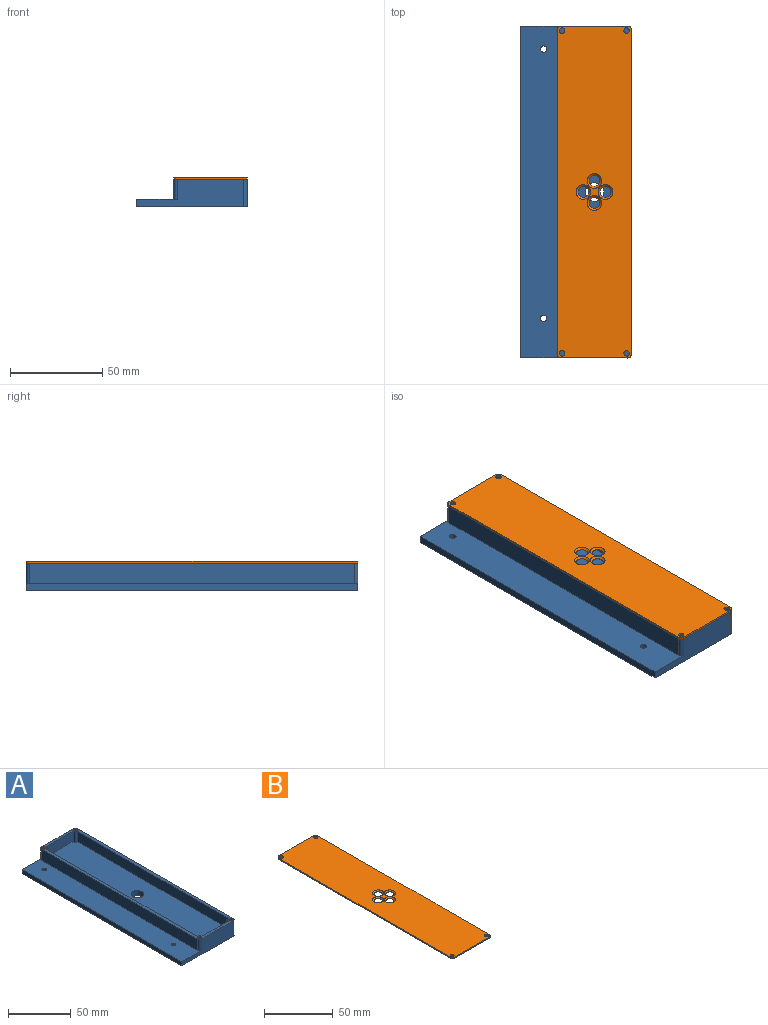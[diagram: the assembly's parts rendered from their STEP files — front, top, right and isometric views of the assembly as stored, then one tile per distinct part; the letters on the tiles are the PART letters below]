
ASSEMBLY  parts=2 mates=1
PART A: 36 faces, bbox 60x180x15 mm
  f0: plane 180x40mm, normal (0,0,1), area 1068.3mm2, adj f1,f3,f4,f7,f10,f11,f12,f13
  f1: plane 58x15mm, normal (0,1,0), area 628mm2, adj f0,f2,f5,f6,f32,f35
  f2: plane 180x4mm, normal (-1,0,0), area 720mm2, adj f1,f3,f5,f6
  f3: plane 58x15mm, normal (0,-1,0), area 628mm2, adj f0,f2,f5,f6,f33,f34
  f4: plane 176x15mm, normal (1,0,0), area 2640mm2, adj f0,f6,f34,f35
  f5: plane 180x22mm, normal (0,0,1), area 3582.5mm2, adj f1,f2,f3,f7,f8,f9,f32,f33
  f6: plane 180x60mm, normal (0,0,-1), area 10700.5mm2, adj f1,f2,f3,f4,f8,f9,f31,f34
  f7: plane 176x11mm, normal (-1,0,0), area 1936mm2, adj f0,f5,f32,f33
  f8: cylinder r=1.75mm len=4mm, axis (0,0,1), area 44mm2, adj f5,f6
  f9: cylinder r=1.75mm len=4mm, axis (0,0,1), area 44mm2, adj f5,f6
  f10: plane 170x10mm, normal (-1,0,0), area 1700mm2, adj f0,f11,f21,f22
  f11: plane 10x2.5mm, normal (0,-1,0), area 25mm2, adj f0,f10,f12,f22
  f12: plane 10x2.5mm, normal (-1,0,0), area 25mm2, adj f0,f11,f13,f22
  f13: plane 30x10mm, normal (0,-1,0), area 300mm2, adj f0,f12,f14,f22
  f14: plane 10x2.5mm, normal (1,0,0), area 25mm2, adj f0,f13,f15,f22
  f15: plane 10x2.5mm, normal (0,-1,0), area 25mm2, adj f0,f14,f16,f22
  f16: plane 170x10mm, normal (1,0,0), area 1700mm2, adj f0,f15,f17,f22
  f17: plane 10x2.5mm, normal (0,1,0), area 25mm2, adj f0,f16,f18,f22
  f18: plane 10x2.5mm, normal (1,0,0), area 25mm2, adj f0,f17,f19,f22
  f19: plane 30x10mm, normal (0,1,0), area 300mm2, adj f0,f18,f20,f22
  f20: plane 10x2.5mm, normal (-1,0,0), area 25mm2, adj f0,f19,f21,f22
  f21: plane 10x2.5mm, normal (0,1,0), area 25mm2, adj f0,f10,f20,f22
  f22: plane 175x35mm, normal (0,0,1), area 6021.5mm2, adj f10,f11,f12,f13,f14,f15,f16,f17
  f23: cylinder r=1.5mm len=9mm, axis (0,0,1), area 84.8mm2, adj f0,f24
  f24: plane 3x3mm, normal (0,0,1), area 7.1mm2, adj f23
  f25: cylinder r=1.5mm len=9mm, axis (0,0,1), area 84.8mm2, adj f0,f26
  f26: plane 3x3mm, normal (0,0,1), area 7.1mm2, adj f25
  f27: cylinder r=1.5mm len=9mm, axis (0,0,1), area 84.8mm2, adj f0,f28
  f28: plane 3x3mm, normal (0,0,1), area 7.1mm2, adj f27
  f29: cylinder r=1.5mm len=9mm, axis (0,0,1), area 84.8mm2, adj f0,f30
  f30: plane 3x3mm, normal (0,0,1), area 7.1mm2, adj f29
  f31: cylinder r=5mm len=10mm, axis (0,0,1), area 157.1mm2, adj f6,f22
  f32: cylinder r=2mm len=11mm, axis (0,0,1), area 34.6mm2, adj f0,f1,f5,f7
  f33: cylinder r=2mm len=11mm, axis (0,0,-1), area 34.6mm2, adj f0,f3,f5,f7
  f34: cylinder r=2mm len=15mm, axis (0,0,1), area 47.1mm2, adj f0,f3,f4,f6
  f35: cylinder r=2mm len=15mm, axis (0,0,-1), area 47.1mm2, adj f0,f1,f4,f6
PART B: 18 faces, bbox 40x180x1 mm
  f0: plane 36x1mm, normal (0,1,0), area 36mm2, adj f4,f5,f6,f9
  f1: plane 176x1mm, normal (-1,0,0), area 176mm2, adj f4,f5,f6,f7
  f2: plane 36x1mm, normal (0,-1,0), area 36mm2, adj f4,f5,f7,f8
  f3: plane 176x1mm, normal (1,0,0), area 176mm2, adj f4,f5,f8,f9
  f4: plane 180x40mm, normal (0,0,1), area 6967.2mm2, adj f0,f1,f2,f3,f6,f7,f8,f9
  f5: plane 180x40mm, normal (0,0,-1), area 7055.2mm2, adj f0,f1,f2,f3,f6,f7,f8,f9
  f6: cylinder r=2mm len=2mm, axis (0,0,1), area 3.1mm2, adj f0,f1,f4,f5
  f7: cylinder r=2mm len=2mm, axis (0,0,-1), area 3.1mm2, adj f1,f2,f4,f5
  f8: cylinder r=2mm len=2mm, axis (0,0,1), area 3.1mm2, adj f2,f3,f4,f5
  f9: cylinder r=2mm len=2mm, axis (0,0,-1), area 3.1mm2, adj f0,f3,f4,f5
  f10: cone r=3mm half-angle=45deg, axis (0,0,1), area 31.1mm2, adj f4,f5
  f11: cone r=3mm half-angle=45deg, axis (0,0,1), area 31.1mm2, adj f4,f5
  f12: cone r=3mm half-angle=45deg, axis (0,0,1), area 31.1mm2, adj f4,f5
  f13: cone r=3mm half-angle=45deg, axis (0,0,1), area 31.1mm2, adj f4,f5
  f14: cylinder r=1.5mm len=3mm, axis (0,0,1), area 9.4mm2, adj f4,f5
  f15: cylinder r=1.5mm len=3mm, axis (0,0,1), area 9.4mm2, adj f4,f5
  f16: cylinder r=1.5mm len=3mm, axis (0,0,1), area 9.4mm2, adj f4,f5
  f17: cylinder r=1.5mm len=3mm, axis (0,0,1), area 9.4mm2, adj f4,f5
PLACE A rot(axis=(0,0,-1),0deg) t=(36.37,-25.56,-118)mm
PLACE B t=(-59.24,-26.12,-103)mm
MATE slider A.f29 <-> B.f15  axis (0,0,1) through (51.34,-118.75,-103)mm
